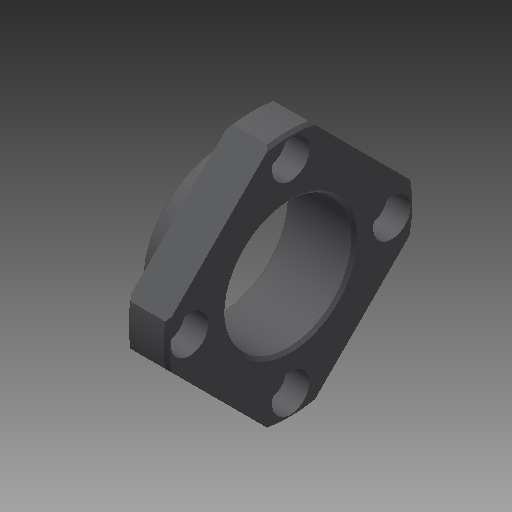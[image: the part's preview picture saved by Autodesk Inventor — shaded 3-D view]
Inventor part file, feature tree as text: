
AUTODESK INVENTOR PART (.ipt)
format: ipt  version: 2018 (Build 220112000, 112)  size: 178,176 bytes
history: native  units: mm
features: other x14, sketch x3, revolve x1, extrude x1, hole x1, pattern_linear x1
ambient origin geometry x8: Origin, YZ Plane, XZ Plane, XY Plane, X Axis, Y Axis, Z Axis, Center Point
bodies: Solid1 (feature_tree)
feature tree (21):
  revolve  "Revolution1"  [1 undecoded]
  extrude  "Extrusion1"  Depth=7.0mm
  hole  "Hole1"  [1 undecoded]
  pattern_linear  "Rectangular Pattern1"  [2 undecoded]
  other  "ff_1_XY"
  other  "ff_1_YZ"
  other  "ff_1_ZX"
  other  "ff_1_X"
  other  "ff_1_Y"
  other  "ff_1_Z"
  other  "ff_1_Center"
  other  "ff_2x_XY"
  other  "ff_2x_YZ"
  other  "ff_2x_ZX"
  other  "ff_2x_X"
  other  "ff_2x_Y"
  other  "ff_2x_Z"
  other  "ff_2x_Center"
  sketch  "Sketch_1"  dims[d0=360.0deg d1=7.0mm d2=0.0mm]
  sketch  "Sketch_2"  dims[d3=3.4mm d4=6.0mm d5=6.5mm d6=4.0mm d7=90.0deg d8=7.0mm d9=0.0mm d10=20.0mm d12=24.748737mm d13=20.0mm d15=24.748737mm]
  sketch  "Sketch3"  dims[d16=0.0mm]
note: 4 required parameter values undecoded (feature->parameter linkage not recoverable at this tier; creation-order binding heuristic only, values carry confidence <= 0.55)